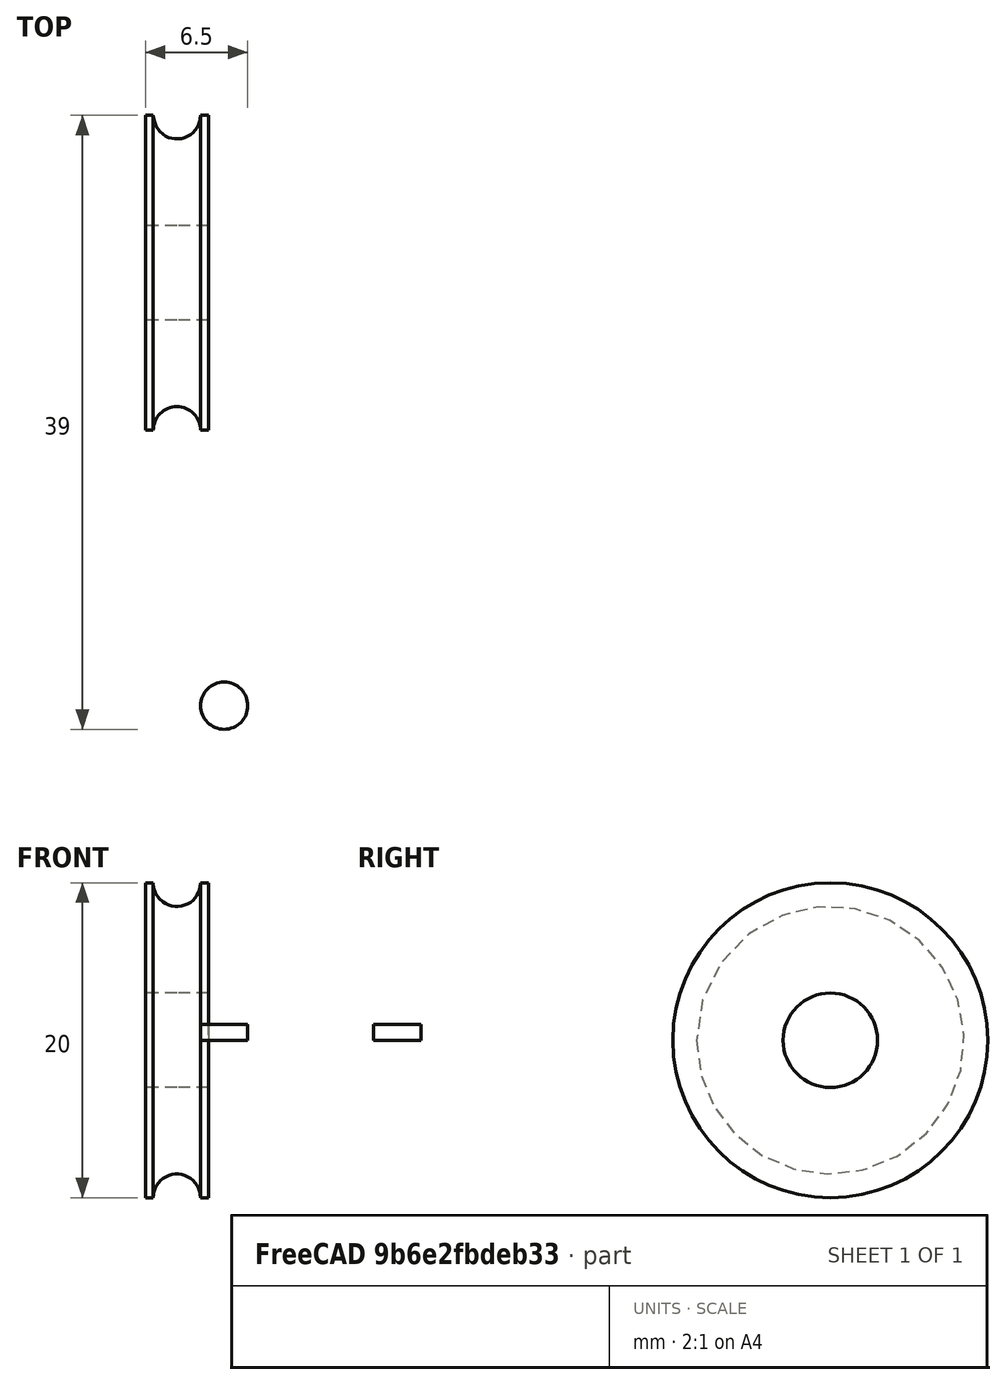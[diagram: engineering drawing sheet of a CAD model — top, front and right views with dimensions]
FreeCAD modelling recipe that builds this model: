
FCSTD DOCUMENT  (FreeCAD 0.19R24415 (Git))
Label: weight_01
License: All rights reserved
LicenseURL: http://en.wikipedia.org/wiki/All_rights_reserved
objects: Part::Part2DObjectPython×10, Part::Revolution×3, Part::MultiFuse×1, Part::Cut×1, Part::Extrusion×1
note: 16 computed .brp shape members not serialized (recipe doc carries the construction recipe); baked Part::Feature solids carry a one-line shape summary decoded from their .brp

FEATURE [Part::Part2DObjectPython] Circle  # Draft 2D object (typed FeaturePython)
  Area = 0
  FirstAngle = 0
  LastAngle = 0
  MakeFace = false
  Placement = pos=(0,30,0) rot=(0.57735,0.57735,0.57735;2.0944rad)
  Radius = 10
FEATURE [Part::Part2DObjectPython] Circle001  # Draft 2D object (typed FeaturePython)
  Area = 0
  FirstAngle = 0
  LastAngle = 0
  MakeFace = false
  Placement = pos=(0,30,0) rot=(0.57735,0.57735,0.57735;2.0944rad)
  Radius = 3
FEATURE [Part::Part2DObjectPython] Rectangle  # Draft 2D object (typed FeaturePython)
  Area = 0
  ChamferSize = 0
  Columns = 1
  FilletRadius = 0
  Height = 7
  Length = 2
  MakeFace = false
  Placement = pos=(-2,20,0) rot=(0,0,1;0rad)
  Rows = 1
FEATURE [Part::Part2DObjectPython] Circle002  # Draft 2D object (typed FeaturePython)
  Area = 0
  FirstAngle = 0
  LastAngle = 0
  MakeFace = false
  Placement = pos=(0,20,0) rot=(0,0,1;0rad)
  Radius = 1.5
FEATURE [Part::Part2DObjectPython] Rectangle001  # Draft 2D object (typed FeaturePython)
  Area = 0
  ChamferSize = 0
  Columns = 1
  FilletRadius = 0
  Height = 7
  Length = 2
  MakeFace = false
  Placement = pos=(0,20,0) rot=(0,0,1;0rad)
  Rows = 1
FEATURE [Part::Revolution] Revolve
  Angle = 360
  Axis = (1,0,0)
  Base = (0,30,0)
  FaceMakerClass = Part::FaceMakerBullseye
  Solid = true
  Source = -> Circle002
  Symmetric = false
FEATURE [Part::Revolution] Revolve001
  Angle = 360
  Axis = (1,0,0)
  Base = (0,30,0)
  FaceMakerClass = Part::FaceMakerBullseye
  Solid = true
  Source = -> Rectangle
  Symmetric = false
FEATURE [Part::Revolution] Revolve002
  Angle = 360
  Axis = (1,0,0)
  Base = (0,30,0)
  FaceMakerClass = Part::FaceMakerBullseye
  Solid = true
  Source = -> Rectangle001
  Symmetric = false
FEATURE [Part::MultiFuse] Fusion
  Shapes = -> [Revolve001,Revolve002]
FEATURE [Part::Cut] Cut
  Base = -> Fusion
  Tool = -> Revolve
FEATURE [Part::Part2DObjectPython] Rectangle002  # Draft 2D object (typed FeaturePython)
  Area = 0
  ChamferSize = 0
  Columns = 1
  FilletRadius = 0
  Height = 10
  Length = 5
  MakeFace = false
  Placement = pos=(0,0,-5) rot=(0.57735,0.57735,0.57735;2.0944rad)
  Rows = 1
FEATURE [Part::Part2DObjectPython] Circle003  # Draft 2D object (typed FeaturePython)
  Area = 0
  FirstAngle = 0
  LastAngle = 0
  MakeFace = false
  Placement = pos=(0,2.5,2) rot=(0.57735,0.57735,0.57735;2.0944rad)
  Radius = 1
FEATURE [Part::Part2DObjectPython] Circle004  # Draft 2D object (typed FeaturePython)
  Area = 0
  FirstAngle = 0
  LastAngle = 0
  MakeFace = false
  Placement = pos=(0,2.5,-2) rot=(0.57735,0.57735,0.57735;2.0944rad)
  Radius = 1
FEATURE [Part::Part2DObjectPython] Rectangle003  # Draft 2D object (typed FeaturePython)
  Area = 0
  ChamferSize = 0
  Columns = 1
  FilletRadius = 0
  Height = 10
  Length = 5
  MakeFace = false
  Placement = pos=(0,0,-30) rot=(0.57735,0.57735,0.57735;2.0944rad)
  Rows = 1
FEATURE [Part::Part2DObjectPython] Circle005  # Draft 2D object (typed FeaturePython)
  Area = 0
  FirstAngle = 0
  LastAngle = 0
  MakeFace = false
  Placement = pos=(3,2.5,0) rot=(0,0,1;0rad)
  Radius = 1.5
FEATURE [Part::Extrusion] Extrude
  Base = -> Circle005
  Dir = (0,0,1)
  DirMode = 2
  FaceMakerClass = Part::FaceMakerBullseye
  LengthFwd = 1
  LengthRev = 0
  Solid = true
  Symmetric = false
